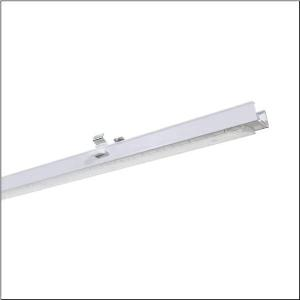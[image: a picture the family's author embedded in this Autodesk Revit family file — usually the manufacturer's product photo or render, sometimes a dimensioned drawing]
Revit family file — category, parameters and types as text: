
# Revit family: trunking_flex_31_51re14ma66b
name_source: partatom
category: Lighting Fixtures
units: mm (PartAtom-declared; Revit-internal decimal feet)

## family parameters
Cut with Voids When Loaded = No
Host = Face
Light Source = No
Part Type = Normal
Room Calculation Point = No
Round Connector Dimension = Use Diameter
Shared = No

## types (1)
- --- (1 x LED, 6400 lm, 40 W, 6500K)
    Apparent Load = 40 VA
    CIE Flux Codes = 72 92 98 99 100
    Color Rendering = 80
    Color Temperature = 6500K
    Default Elevation = 1800 mm
    Description = Trunking Flex 31, luminaire insert, of extruded aluminium section, coated, traffic white (RAL 9016), length: 1.172mm, width: 91mm, height: 53mm, LED rated luminous flux: 6.400lm, light colour: 865, SDCM (Standard Deviation of Colour Matching)MacAdam ≤ 3 SDCM (initial), control gear: ON/OFF Multilumen, with system connector: socket, mains connection: 220..240V, AC, 50/60Hz, rated input power: 40W, luminous flux adjustable on luminaire in four steps (3420/4540/5580/6630lm), connected load according to luminous flux setting (20/26/33/40W), primary light control with lens, of plastic, primary optical cover: cover, of PMMA, light emission: direct distribution, primary light characteristic: asymmetric, protection rating (complete): IP20, insulation class (complete): insulation class I (protective earthing), certification: CE, UKCA, impact resistance: IK02, permissible ambient temperature for indoor applications: -20..+40°C, packaging unit: 1 piece
    Height = 58 mm
    Lamp = 1 x LED
    Lamp Light Flux = 6400 lm
    Lamp Power = 40 W
    Lamp count = 1
    Length = 1172 mm
    Luminous efficacy = 160 lm/W
    Manufacturer = Siteco
    ModVariant = No
    Model = 51RE14MA66B
    Mounting Place = Ceiling
    Mounting Type = Pendant
    Number of Poles = 1
    OnlyDefault = Yes
    Power Factor = 1
    Product Name = Trunking Flex 31
    Product group = luminaire insert | ceiling pendant
    ProductGroupID = 901
    Protection Class = Protection class I
    Protection Degree = IP 20
    RLX_Detail_Level = 1
    RLX_Emergency_Light_Flux = 0 lm
    RLX_Emergency_Type = 0
    RLX_Emergency_Type_DB = No
    RlxData = <blob elided: 20745 chars, md5=4acaafb3>
    Socket = socket
    Standby Power = 0 W
    System Light Flux = 6400 lm
    System Power = 40 W
    Type Comments = factory setting: luminous flux: 100 % | (ON | ON) | 300 mA
    Type Image = l_1266702.jpg
    URL = http://relux.com
    VarID = @adj_067191
    Voltage = 0 V
    Weight = 0.00 kg
    Width = 65 mm

## geometry (parser evidence)
native form markers: Blend x4, Sweep x11
no freeform markers — native parametric forms only
